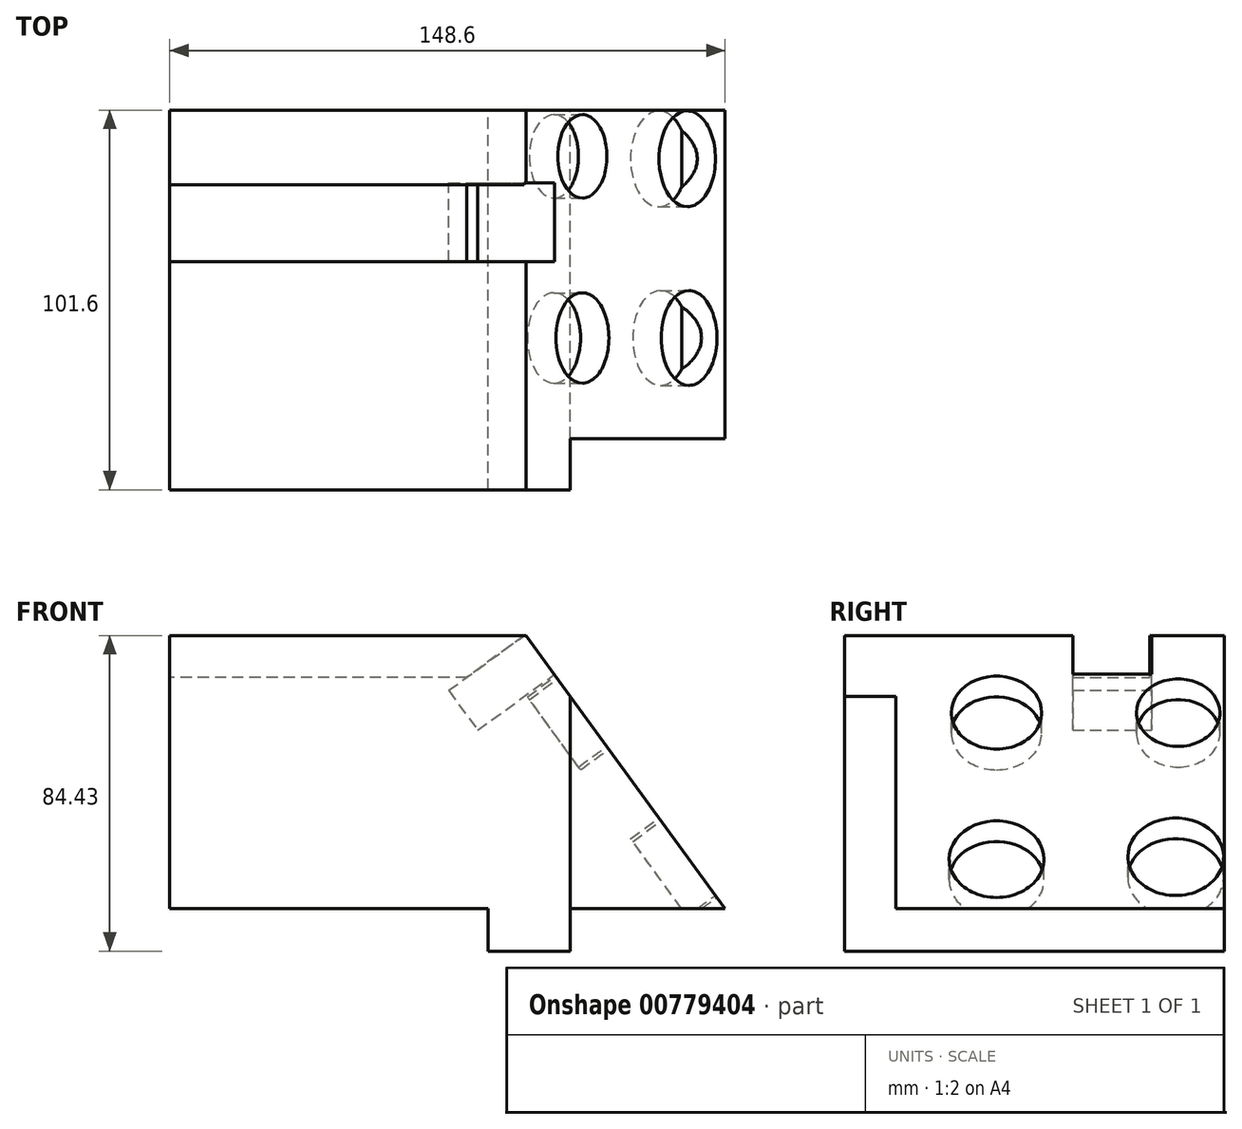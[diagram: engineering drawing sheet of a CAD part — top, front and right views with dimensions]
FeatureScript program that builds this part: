
annotation { "Feature Type Name" : "Feature", "Feature Type Description" : "" }
export const myFeature = defineFeature(function(context is Context, id is Id, definition is map)
    precondition{}
    {
        {
            var Q0;
            Q0=qCreatedBy(makeId("Front.planeOp"),FACE);
            var sketch = newSketch(context, id + "F0", { "sketchPlane" : qUnion([Q0])});
            skLineSegment(sketch, "E0.bottom", {"start": v(-63.3, 39.24) * mm, "end": v(32.1, 39.24) * mm});
            skLineSegment(sketch, "E0.top", {"start": v(-63.3, -33.83) * mm, "end": v(21.88, -33.83) * mm});
            skLineSegment(sketch, "E0.left", {"start": v(-63.3, 39.24) * mm, "end": v(-63.3, -33.83) * mm});
            skLineSegment(sketch, "E1", {"start": v(32.1, 39.24) * mm, "end": v(85.3, -33.83) * mm});
            skLineSegment(sketch, "E2", {"start": v(85.3, -33.83) * mm, "end": v(43.9, -33.83) * mm});
            skLineSegment(sketch, "E3.top", {"start": v(43.9, -45.19) * mm, "end": v(21.88, -45.19) * mm});
            skLineSegment(sketch, "E3.left", {"start": v(43.9, -33.83) * mm, "end": v(43.9, -45.19) * mm});
            skLineSegment(sketch, "E3.right", {"start": v(21.88, -33.83) * mm, "end": v(21.88, -45.19) * mm});
            skPoint(sketch, "E4.orphan", {"position": v(32.1, -33.83) * mm});
            skSolve(sketch);
        }
        {
            var Q0;
            Q0 = qSketchRegion(id + "F0", true);
            extrude(context, id + "F1", {"entities" : qUnion([Q0]), "depth" : 101.6 * mm, "offsetDistance" : 25.4 * mm});
        }
        {
            var Q0;
            Q0=makeQuery(id+"F1.opExtrude","SWEPT_FACE",FACE,{"disambiguationData":[OSD([sQuery(id+"F0.wireOp",EDGE,"E0.bottom")])]});
            var sketch = newSketch(context, id + "F2", { "sketchPlane" : qUnion([Q0])});
            skLineSegment(sketch, "E5.bottom", {"start": v(32.1, -19.95) * mm, "end": v(-63.3, -19.95) * mm});
            skLineSegment(sketch, "E5.top", {"start": v(32.1, -40.51) * mm, "end": v(-63.3, -40.51) * mm});
            skLineSegment(sketch, "E5.left", {"start": v(32.1, -19.95) * mm, "end": v(32.1, -40.51) * mm});
            skLineSegment(sketch, "E5.right", {"start": v(-63.3, -19.95) * mm, "end": v(-63.3, -40.51) * mm});
            skSolve(sketch);
        }
        {
            var Q0;
            Q0=makeQuery(id+"F2.imprint","IMPRINT",FACE,{"disambiguationData":[TD([[makeQuery(id+"F2.imprint","IMPRINT",EDGE,{"derivedFrom":sQuery(id+"F2.wireOp",EDGE,"E5.bottom")}),1.0]])]});
            extrude(context, id + "F3", {"entities" : qUnion([Q0]), "operationType" : NewBodyOperationType.REMOVE, "oppositeDirection" : true, "depth" : 11.18 * mm, "offsetDistance" : 25.4 * mm});
        }
        {
            var Q0;
            Q0=makeQuery(id+"F1.opExtrude","SWEPT_FACE",FACE,{"disambiguationData":[OSD([sQuery(id+"F0.wireOp",EDGE,"E1")])]});
            var sketch = newSketch(context, id + "F4", { "sketchPlane" : qUnion([Q0])});
            skSolve(sketch);
        }
        {
            var Q0;
            {var subQ1=sQuery(id+"F0.wireOp",EDGE,"E1");Q0=makeQuery(id+"F4.imprint","IMPRINT",FACE,{"disambiguationData":[TD([[makeQuery(id+"F4.imprint","IMPRINT",EDGE,{"derivedFrom":makeQuery(id+"F1.opExtrude","CAP_EDGE",EDGE,{"disambiguationData":[OSD([subQ1])],"isStart":true})}),-1.0]])]});}
            var sketch = newSketch(context, id + "F5", { "sketchPlane" : qUnion([Q0])});
            skLineSegment(sketch, "E6.bottom", {"start": v(-40.56, 13.15) * mm, "end": v(-19.5, 13.15) * mm});
            skLineSegment(sketch, "E6.top", {"start": v(-40.56, 0) * mm, "end": v(-19.5, 0) * mm});
            skLineSegment(sketch, "E6.left", {"start": v(-40.56, 13.15) * mm, "end": v(-40.56, 0) * mm});
            skLineSegment(sketch, "E6.right", {"start": v(-19.5, 13.15) * mm, "end": v(-19.5, 0) * mm});
            skSolve(sketch);
        }
        {
            var Q0;
            Q0 = qSketchRegion(id + "F5", true);
            extrude(context, id + "F6", {"entities" : qUnion([Q0]), "operationType" : NewBodyOperationType.REMOVE, "oppositeDirection" : true, "depth" : 25.4 * mm, "offsetDistance" : 25.4 * mm});
        }
        {
            var Q0;
            {var subQ1=sQuery(id+"F0.wireOp",EDGE,"E1");Q0=makeQuery(id+"F4.imprint","IMPRINT",FACE,{"disambiguationData":[TD([[makeQuery(id+"F4.imprint","IMPRINT",EDGE,{"derivedFrom":makeQuery(id+"F1.opExtrude","CAP_EDGE",EDGE,{"disambiguationData":[OSD([subQ1])],"isStart":true})}),-1.0]])]});}
            var sketch = newSketch(context, id + "F7", { "sketchPlane" : qUnion([Q0])});
            skCircle(sketch, "E7", {"center": v(-60.96, -12.67) * mm, "radius": 12.1 * mm});
            skCircle(sketch, "E8", {"center": v(-12.38, -12.67) * mm, "radius": 11.16 * mm});
            skCircle(sketch, "E9", {"center": v(-60.96, -61.15) * mm, "radius": 12.69 * mm});
            skCircle(sketch, "E10", {"center": v(-13.02, -60.35) * mm, "radius": 12.83 * mm});
            skSolve(sketch);
        }
        {
            var Q0;
            Q0 = qSketchRegion(id + "F7", true);
            extrude(context, id + "F8", {"entities" : qUnion([Q0]), "operationType" : NewBodyOperationType.REMOVE, "oppositeDirection" : true, "depth" : 9.4 * mm, "offsetDistance" : 25.4 * mm});
        }
        {
            var Q0;
            Q0=makeQuery(id+"F1.opExtrude","CAP_FACE",FACE,{"disambiguationData":[OSD([sQuery(id+"F0.wireOp",EDGE,"E0.bottom"),sQuery(id+"F0.wireOp",EDGE,"E0.top"),sQuery(id+"F0.wireOp",EDGE,"E0.left"),sQuery(id+"F0.wireOp",EDGE,"E1"),sQuery(id+"F0.wireOp",EDGE,"E2"),sQuery(id+"F0.wireOp",EDGE,"E3.top"),sQuery(id+"F0.wireOp",EDGE,"E3.left"),sQuery(id+"F0.wireOp",EDGE,"E3.right")])],"isStart":false});
            var sketch = newSketch(context, id + "F9", { "sketchPlane" : qUnion([Q0])});
            skLineSegment(sketch, "E11", {"start": v(43.9, -33.83) * mm, "end": v(43.9, 31.83) * mm});
            skLineSegment(sketch, "E12", {"start": v(43.9, 31.83) * mm, "end": v(85.3, -33.83) * mm});
            skLineSegment(sketch, "E13", {"start": v(85.3, -33.83) * mm, "end": v(43.9, -33.83) * mm});
            skSolve(sketch);
        }
        {
            var Q0;
            Q0 = qSketchRegion(id + "F9", true);
            extrude(context, id + "F10", {"entities" : qUnion([Q0]), "operationType" : NewBodyOperationType.REMOVE, "oppositeDirection" : true, "depth" : 13.72 * mm, "offsetDistance" : 25.4 * mm});
        }
    });
